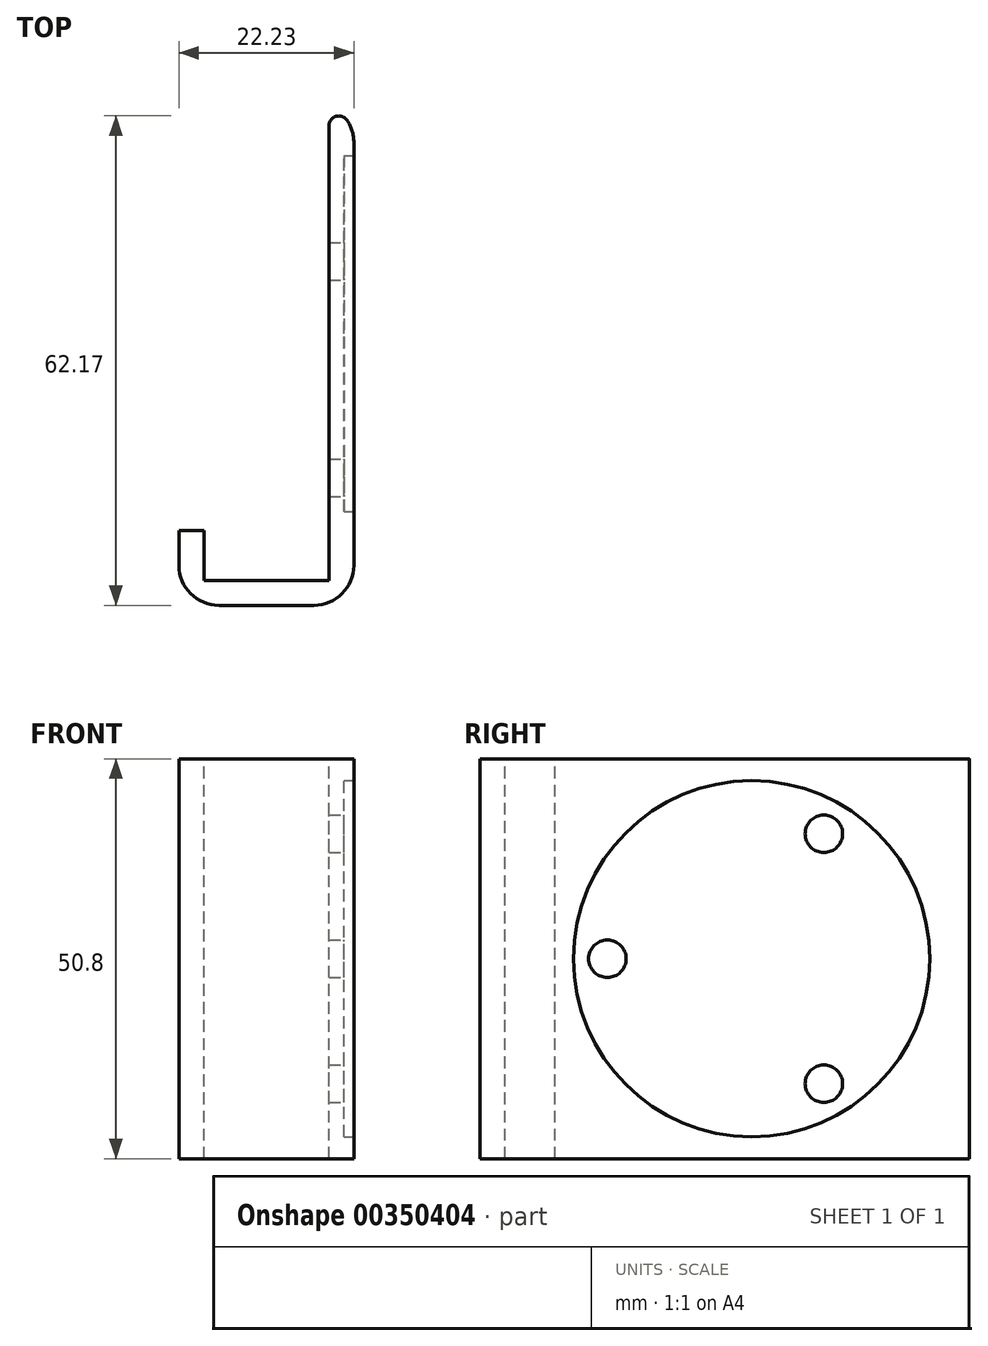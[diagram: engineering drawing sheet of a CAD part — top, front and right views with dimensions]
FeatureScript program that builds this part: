
annotation { "Feature Type Name" : "Feature", "Feature Type Description" : "" }
export const myFeature = defineFeature(function(context is Context, id is Id, definition is map)
    precondition{}
    {
        {
            var Q0;
            Q0=qCreatedBy(makeId("Right.planeOp"),FACE);
            var sketch = newSketch(context, id + "F0", { "sketchPlane" : qUnion([Q0])});
            skLineSegment(sketch, "E0.bottom", {"start": v(31.75, 25.4) * mm, "end": v(-31.75, 25.4) * mm});
            skLineSegment(sketch, "E0.top", {"start": v(31.75, -25.4) * mm, "end": v(-31.75, -25.4) * mm});
            skLineSegment(sketch, "E0.left", {"start": v(31.75, 25.4) * mm, "end": v(31.75, -25.4) * mm});
            skLineSegment(sketch, "E0.right", {"start": v(-31.75, 25.4) * mm, "end": v(-31.75, -25.4) * mm});
            skPoint(sketch, "E0.middle", {"position": v(0, 0) * mm});
            skSolve(sketch);
        }
        {
            var Q0;
            Q0 = qSketchRegion(id + "F0", true);
            extrude(context, id + "F1", {"entities" : qUnion([Q0]), "depth" : 3.17 * mm});
        }
        {
            var Q0;
            Q0=makeQuery(id+"F1.opExtrude","CAP_FACE",FACE,{"disambiguationData":[OSD([sQuery(id+"F0.wireOp",EDGE,"E0.bottom"),sQuery(id+"F0.wireOp",EDGE,"E0.top"),sQuery(id+"F0.wireOp",EDGE,"E0.left"),sQuery(id+"F0.wireOp",EDGE,"E0.right")])],"isStart":false});
            var sketch = newSketch(context, id + "F2", { "sketchPlane" : qUnion([Q0])});
            skCircle(sketch, "E1", {"center": v(2.78, 0) * mm, "radius": 22.62 * mm});
            skSolve(sketch);
        }
        {
            var Q0;
            Q0=makeQuery(id+"F2.imprint","IMPRINT",FACE,{"disambiguationData":[TD([[makeQuery(id+"F2.imprint","IMPRINT",EDGE,{"derivedFrom":sQuery(id+"F2.wireOp",EDGE,"E1")}),1.0]])]});
            extrude(context, id + "F3", {"entities" : qUnion([Q0]), "operationType" : NewBodyOperationType.REMOVE, "oppositeDirection" : true, "depth" : 1.27 * mm});
        }
        {
            var Q0;
            Q0=makeQuery(id+"F3.boolean.opBoolean","COPY",FACE,{"derivedFrom":makeQuery(id+"F3.opExtrude","CAP_FACE",FACE,{"disambiguationData":[OSD([sQuery(id+"F2.wireOp",EDGE,"E1")])],"isStart":false})});
            var sketch = newSketch(context, id + "F4", { "sketchPlane" : qUnion([Q0])});
            skCircle(sketch, "E2", {"center": v(-15.55, 0) * mm, "radius": 2.38 * mm});
            skCircle(sketch, "E3", {"center": v(11.94, 15.88) * mm, "radius": 2.38 * mm});
            skCircle(sketch, "E4", {"center": v(11.94, -15.88) * mm, "radius": 2.38 * mm});
            skLineSegment(sketch, "E5", {"start": v(2.78, 0) * mm, "end": v(11.94, 15.88) * mm});
            skLineSegment(sketch, "E6", {"start": v(2.78, 0) * mm, "end": v(11.94, -15.88) * mm});
            skLineSegment(sketch, "E7", {"start": v(2.78, 0) * mm, "end": v(-15.55, 0) * mm});
            skLineSegment(sketch, "E8", {"start": v(-15.55, 0) * mm, "end": v(11.94, 15.88) * mm});
            skLineSegment(sketch, "E9", {"start": v(11.94, -15.88) * mm, "end": v(11.94, 15.88) * mm});
            skLineSegment(sketch, "E10", {"start": v(11.94, -15.88) * mm, "end": v(-15.55, 0) * mm});
            skSolve(sketch);
        }
        {
            var Q0;
            {var subQ0=sQuery(id+"F4.wireOp",EDGE,"E8");var subQ1=sQuery(id+"F4.wireOp",EDGE,"E3");var subQ2=makeQuery(id+"F4.imprint","INTERSECT",VERTEX,{"derivedFrom":[subQ1,subQ0]});Q0=makeQuery(id+"F4.imprint","IMPRINT",FACE,{"disambiguationData":[TD([[makeQuery(id+"F4.imprint","IMPRINT",EDGE,{"disambiguationData":[TD([[subQ2,1.0]])],"derivedFrom":subQ1}),1.0]])]});}
            var Q1;
            {var subQ0=sQuery(id+"F4.wireOp",EDGE,"E8");var subQ1=sQuery(id+"F4.wireOp",EDGE,"E2");var subQ2=makeQuery(id+"F4.imprint","INTERSECT",VERTEX,{"derivedFrom":[subQ1,subQ0]});Q1=makeQuery(id+"F4.imprint","IMPRINT",FACE,{"disambiguationData":[TD([[makeQuery(id+"F4.imprint","IMPRINT",EDGE,{"disambiguationData":[TD([[subQ2,-1.0]])],"derivedFrom":subQ1}),1.0]])]});}
            var Q2;
            {var subQ0=sQuery(id+"F4.wireOp",EDGE,"E7");var subQ1=sQuery(id+"F4.wireOp",EDGE,"E2");var subQ2=makeQuery(id+"F4.imprint","INTERSECT",VERTEX,{"derivedFrom":[subQ1,subQ0]});Q2=makeQuery(id+"F4.imprint","IMPRINT",FACE,{"disambiguationData":[TD([[makeQuery(id+"F4.imprint","IMPRINT",EDGE,{"disambiguationData":[TD([[subQ2,1.0]])],"derivedFrom":subQ1}),1.0]])]});}
            var Q3;
            {var subQ0=sQuery(id+"F4.wireOp",EDGE,"E8");var subQ1=sQuery(id+"F4.wireOp",EDGE,"E2");var subQ2=makeQuery(id+"F4.imprint","INTERSECT",VERTEX,{"derivedFrom":[subQ1,subQ0]});Q3=makeQuery(id+"F4.imprint","IMPRINT",FACE,{"disambiguationData":[TD([[makeQuery(id+"F4.imprint","IMPRINT",EDGE,{"disambiguationData":[TD([[subQ2,1.0]])],"derivedFrom":subQ1}),1.0]])]});}
            var Q4;
            {var subQ0=sQuery(id+"F4.wireOp",EDGE,"E6");var subQ1=sQuery(id+"F4.wireOp",EDGE,"E4");var subQ2=makeQuery(id+"F4.imprint","INTERSECT",VERTEX,{"derivedFrom":[subQ1,subQ0]});Q4=makeQuery(id+"F4.imprint","IMPRINT",FACE,{"disambiguationData":[TD([[makeQuery(id+"F4.imprint","IMPRINT",EDGE,{"disambiguationData":[TD([[subQ2,-1.0]])],"derivedFrom":subQ1}),1.0]])]});}
            var Q5;
            {var subQ0=sQuery(id+"F4.wireOp",EDGE,"E5");var subQ1=sQuery(id+"F4.wireOp",EDGE,"E3");var subQ2=makeQuery(id+"F4.imprint","INTERSECT",VERTEX,{"derivedFrom":[subQ1,subQ0]});Q5=makeQuery(id+"F4.imprint","IMPRINT",FACE,{"disambiguationData":[TD([[makeQuery(id+"F4.imprint","IMPRINT",EDGE,{"disambiguationData":[TD([[subQ2,-1.0]])],"derivedFrom":subQ1}),1.0]])]});}
            var Q6;
            {var subQ0=sQuery(id+"F4.wireOp",EDGE,"E5");var subQ1=sQuery(id+"F4.wireOp",EDGE,"E3");var subQ2=makeQuery(id+"F4.imprint","INTERSECT",VERTEX,{"derivedFrom":[subQ1,subQ0]});Q6=makeQuery(id+"F4.imprint","IMPRINT",FACE,{"disambiguationData":[TD([[makeQuery(id+"F4.imprint","IMPRINT",EDGE,{"disambiguationData":[TD([[subQ2,1.0]])],"derivedFrom":subQ1}),1.0]])]});}
            var Q7;
            {var subQ0=sQuery(id+"F4.wireOp",EDGE,"E9");var subQ1=sQuery(id+"F4.wireOp",EDGE,"E4");var subQ2=makeQuery(id+"F4.imprint","INTERSECT",VERTEX,{"derivedFrom":[subQ1,subQ0]});Q7=makeQuery(id+"F4.imprint","IMPRINT",FACE,{"disambiguationData":[TD([[makeQuery(id+"F4.imprint","IMPRINT",EDGE,{"disambiguationData":[TD([[subQ2,1.0]])],"derivedFrom":subQ1}),1.0]])]});}
            var Q8;
            {var subQ0=sQuery(id+"F4.wireOp",EDGE,"E6");var subQ1=sQuery(id+"F4.wireOp",EDGE,"E4");var subQ2=makeQuery(id+"F4.imprint","INTERSECT",VERTEX,{"derivedFrom":[subQ1,subQ0]});Q8=makeQuery(id+"F4.imprint","IMPRINT",FACE,{"disambiguationData":[TD([[makeQuery(id+"F4.imprint","IMPRINT",EDGE,{"disambiguationData":[TD([[subQ2,1.0]])],"derivedFrom":subQ1}),1.0]])]});}
            extrude(context, id + "F5", {"entities" : qUnion([Q0, Q1, Q2, Q3, Q4, Q5, Q6, Q7, Q8]), "operationType" : NewBodyOperationType.REMOVE, "oppositeDirection" : true, "depth" : 25.4 * mm});
        }
        {
            var Q0;
            Q0=makeQuery(id+"F1.opExtrude","SWEPT_FACE",FACE,{"disambiguationData":[OSD([sQuery(id+"F0.wireOp",EDGE,"E0.bottom")])]});
            var sketch = newSketch(context, id + "F6", { "sketchPlane" : qUnion([Q0])});
            skLineSegment(sketch, "E11", {"start": v(0, -31.75) * mm, "end": v(-19.05, -31.75) * mm});
            skLineSegment(sketch, "E12", {"start": v(-19.05, -31.75) * mm, "end": v(-19.05, -22.23) * mm});
            skLineSegment(sketch, "E13", {"start": v(-19.05, -22.23) * mm, "end": v(-15.88, -22.23) * mm});
            skLineSegment(sketch, "E14", {"start": v(-15.88, -22.23) * mm, "end": v(-15.88, -28.58) * mm});
            skLineSegment(sketch, "E15", {"start": v(-15.88, -28.58) * mm, "end": v(0, -28.58) * mm});
            skSolve(sketch);
        }
        {
            var Q0;
            {var subQ0=sQuery(id+"F6.wireOp",EDGE,"E11");Q0=makeQuery(id+"F6.imprint","IMPRINT",FACE,{"disambiguationData":[TD([[makeQuery(id+"F6.imprint","IMPRINT",EDGE,{"derivedFrom":subQ0}),-1.0]])]});}
            var Q1;
            Q1=makeQuery(id+"F1.opExtrude","SWEPT_FACE",FACE,{"disambiguationData":[OSD([sQuery(id+"F0.wireOp",EDGE,"E0.top")])]});
            extrude(context, id + "F7", {"entities" : qUnion([Q0]), "operationType" : NewBodyOperationType.ADD, "endBound" : BoundingType.UP_TO_SURFACE, "oppositeDirection" : true, "endBoundEntityFace" : qUnion([Q1]), "depth" : 25.4 * mm});
        }
        {
            var Q0;
            Q0=makeQuery(id+"F7.opExtrude","SWEPT_EDGE",EDGE,{"disambiguationData":[OSD([sQuery(id+"F0.wireOp",EDGE,"E0.bottom"),sQuery(id+"F6.wireOp",EDGE,"E15")])]});
            var Q1;
            Q1=makeQuery(id+"F7.opExtrude","SWEPT_EDGE",EDGE,{"disambiguationData":[OSD([sQuery(id+"F6.wireOp",EDGE,"E11"),sQuery(id+"F6.wireOp",EDGE,"E12")])]});
            var Q2;
            Q2=makeQuery(id+"F1.opExtrude","CAP_EDGE",EDGE,{"disambiguationData":[OSD([sQuery(id+"F0.wireOp",EDGE,"E0.left")])],"isStart":false});
            fillet(context, id + "F8", {"entities" : qUnion([Q0, Q1, Q2]), "radius" : 5.08 * mm, "tangentPropagation" : true, "allowEdgeOverflow" : false});
        }
        {
            var Q0;
            Q0=makeQuery(id+"F1.opExtrude","CAP_EDGE",EDGE,{"disambiguationData":[OSD([sQuery(id+"F0.wireOp",EDGE,"E0.right")])],"isStart":false});
            fillet(context, id + "F9", {"entities" : qUnion([Q0]), "radius" : 5.08 * mm, "tangentPropagation" : true, "allowEdgeOverflow" : false});
        }
        {
            var Q0;
            {var subQ0=sQuery(id+"F0.wireOp",EDGE,"E0.left");Q0=makeQuery(id+"F8.opFillet","BLEND_EDGE",EDGE,{"blendedFrom":[makeQuery(id+"F1.opExtrude","CAP_EDGE",EDGE,{"disambiguationData":[OSD([subQ0])],"isStart":false}),makeQuery(id+"F1.opExtrude","CAP_FACE",FACE,{"disambiguationData":[OSD([sQuery(id+"F0.wireOp",EDGE,"E0.bottom"),sQuery(id+"F0.wireOp",EDGE,"E0.top"),subQ0,sQuery(id+"F0.wireOp",EDGE,"E0.right")])],"isStart":true})],"blendedInto":[makeQuery(id+"F1.opExtrude","CAP_FACE",FACE,{"disambiguationData":[OSD([sQuery(id+"F0.wireOp",EDGE,"E0.bottom"),sQuery(id+"F0.wireOp",EDGE,"E0.top"),subQ0,sQuery(id+"F0.wireOp",EDGE,"E0.right")])],"isStart":true})]});}
            fillet(context, id + "F10", {"entities" : qUnion([Q0]), "radius" : 1.27 * mm, "tangentPropagation" : true, "allowEdgeOverflow" : false});
        }
    });
